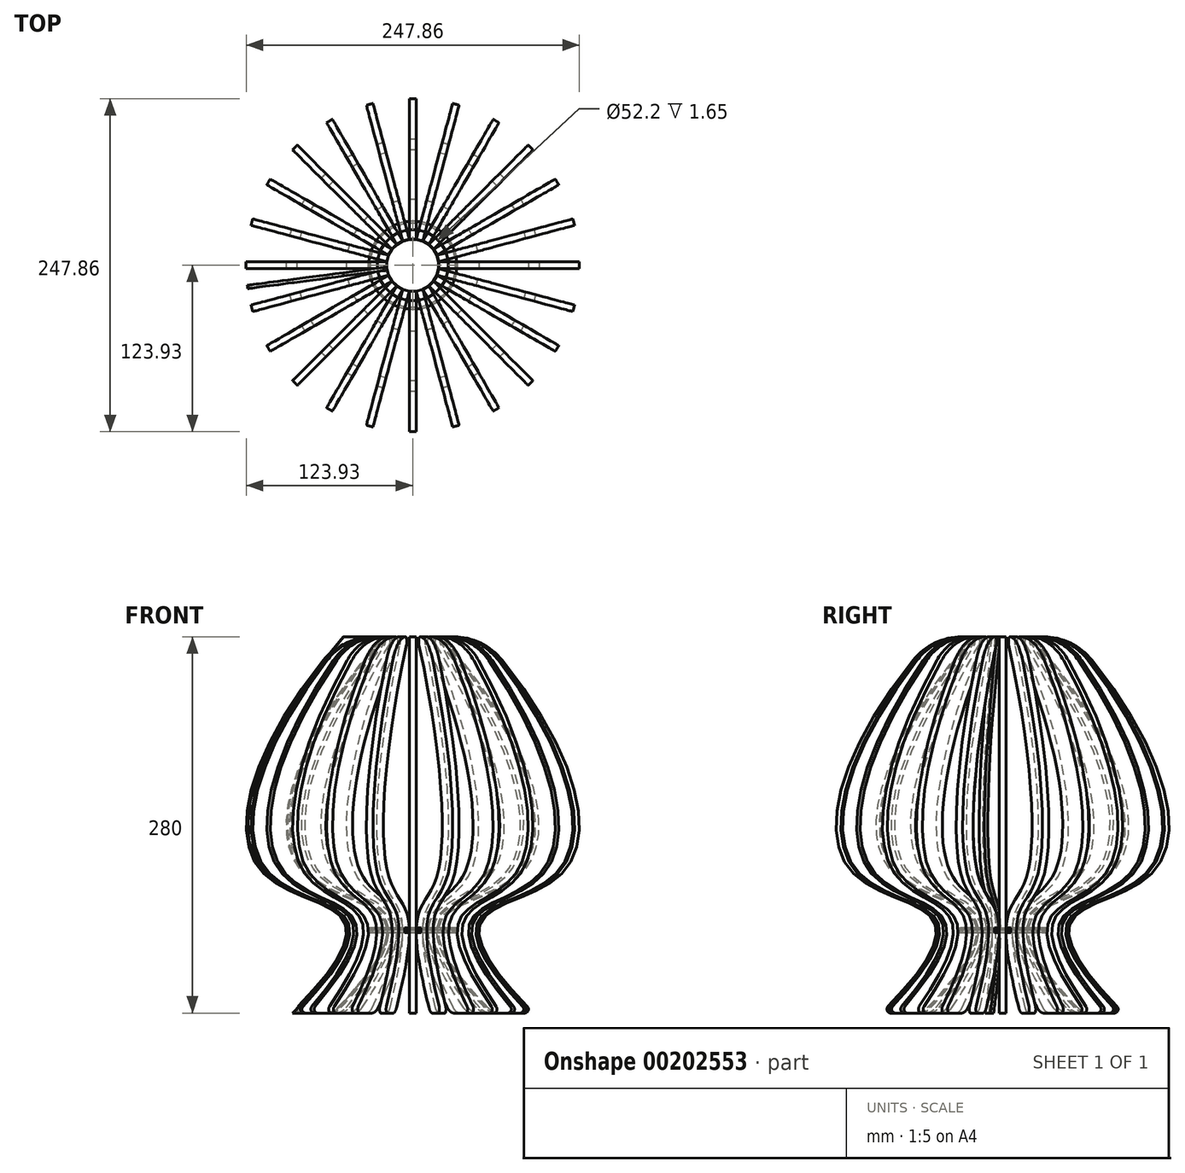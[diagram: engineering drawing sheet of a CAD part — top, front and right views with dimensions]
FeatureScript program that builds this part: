
annotation { "Feature Type Name" : "Feature", "Feature Type Description" : "" }
export const myFeature = defineFeature(function(context is Context, id is Id, definition is map)
    precondition{}
    {
        {
            var Q0;
            Q0=qCreatedBy(makeId("Top.planeOp"),FACE);
            var sketch = newSketch(context, id + "F0", { "sketchPlane" : qUnion([Q0])});
            skCircle(sketch, "E0", {"center": v(0, 0) * mm, "radius": 32.75 * mm});
            skCircle(sketch, "E1", {"center": v(0, 0) * mm, "radius": 26.1 * mm});
            skSolve(sketch);
        }
        {
            var Q0;
            Q0=qSketchRegion(id+"F0",true);
            extrude(context, id + "F1", {"entities" : qUnion([Q0]), "depth" : 1.65 * mm});
        }
        {
            var Q0;
            Q0=makeQuery(id+"F1.opExtrude","CAP_FACE",FACE,{"disambiguationData":[OSD([sQuery(id+"F0.wireOp",EDGE,"E0"),sQuery(id+"F0.wireOp",EDGE,"E1")])],"isStart":false});
            var sketch = newSketch(context, id + "F2", { "sketchPlane" : qUnion([Q0])});
            skLineSegment(sketch, "E2.bottom", {"start": v(2.5, -26.5) * mm, "end": v(-2.5, -26.5) * mm});
            skLineSegment(sketch, "E2.top", {"start": v(2.5, -31.5) * mm, "end": v(-2.5, -31.5) * mm});
            skLineSegment(sketch, "E2.left", {"start": v(2.5, -26.5) * mm, "end": v(2.5, -31.5) * mm});
            skLineSegment(sketch, "E2.right", {"start": v(-2.5, -26.5) * mm, "end": v(-2.5, -31.5) * mm});
            skPoint(sketch, "E2.middle", {"position": v(0, -29) * mm});
            skSolve(sketch);
        }
        {
            var Q0;
            Q0=makeQuery(id+"F2.imprint","IMPRINT",FACE,{"disambiguationData":[TD([[makeQuery(id+"F2.imprint","IMPRINT",EDGE,{"derivedFrom":sQuery(id+"F2.wireOp",EDGE,"E2.bottom")}),1.0]])]});
            extrude(context, id + "F3", {"entities" : qUnion([Q0]), "depth" : 1.62 * mm});
        }
        {
            var Q0;
            Q0=makeQuery(id+"F3.opExtrude","SWEPT_BODY",BODY,{"disambiguationData":[OSD([sQuery(id+"F2.wireOp",EDGE,"E2.bottom"),sQuery(id+"F2.wireOp",EDGE,"E2.top"),sQuery(id+"F2.wireOp",EDGE,"E2.left"),sQuery(id+"F2.wireOp",EDGE,"E2.right")])]});
            var Q1;
            Q1=makeQuery(id+"F1.opExtrude","CAP_EDGE",EDGE,{"disambiguationData":[OSD([sQuery(id+"F0.wireOp",EDGE,"E0")])],"isStart":false});
            circularPattern(context, id + "F4", {"entities" : qUnion([Q0]), "axis" : qUnion([Q1]), "angle" : 360 * degree, "instanceCount" : 24, "equalSpace" : true});
        }
        {
            var Q0;
            Q0=qCreatedBy(makeId("Front.planeOp"),FACE);
            var sketch = newSketch(context, id + "F5", { "sketchPlane" : qUnion([Q0])});
            skFitSpline(sketch, "E3", {"points": [v(-52, 220) * mm, v(-112, 45) * mm, v(-52, 10) * mm, v(-90, -60) * mm], "startDerivative": vector(-464.56, -534.92) * mm, "endDerivative": vector(-310.1, -311.21) * mm});
            skLineSegment(sketch, "E4", {"start": v(-9.97, -59.99) * mm, "end": v(-9.97, -0.01) * mm, "construction": true});
            skLineSegment(sketch, "E5", {"start": v(-9.97, -0.01) * mm, "end": v(-33, -0.01) * mm});
            skLineSegment(sketch, "E6", {"start": v(-33, -0.01) * mm, "end": v(-33, 3.46) * mm});
            skLineSegment(sketch, "E7", {"start": v(-33, 3.46) * mm, "end": v(0, 3.46) * mm});
            skLineSegment(sketch, "E8", {"start": v(0, 3.46) * mm, "end": v(0, 369.62) * mm, "construction": true});
            skLineSegment(sketch, "E9", {"start": v(-22, 3.46) * mm, "end": v(-22, 220) * mm, "construction": true});
            skFitSpline(sketch, "E10", {"points": [v(-60, -60) * mm, v(-22, 10) * mm, v(-82, 45) * mm, v(-22, 220) * mm], "startDerivative": vector(310.1, 311.21) * mm, "endDerivative": vector(464.56, 534.92) * mm});
            skLineSegment(sketch, "E11", {"start": v(-90, -60) * mm, "end": v(-60, -60) * mm});
            skLineSegment(sketch, "E12", {"start": v(-60.1, -30) * mm, "end": v(-30.1, -30) * mm, "construction": true});
            skLineSegment(sketch, "E13", {"start": v(-52, 10) * mm, "end": v(-22, 10) * mm, "construction": true});
            skLineSegment(sketch, "E14", {"start": v(-52, 220) * mm, "end": v(-22, 220) * mm});
            skLineSegment(sketch, "E15", {"start": v(-120.25, 141.41) * mm, "end": v(-90.25, 141.41) * mm, "construction": true});
            skLineSegment(sketch, "E16", {"start": v(-112, 45) * mm, "end": v(-82, 45) * mm, "construction": true});
            skPoint(sketch, "E17", {"position": v(-9.97, -30) * mm});
            skSolve(sketch);
        }
        {
            var Q0;
            Q0=makeQuery(id+"F5.imprint","IMPRINT",FACE,{"disambiguationData":[TD([[makeQuery(id+"F5.imprint","IMPRINT",EDGE,{"derivedFrom":sQuery(id+"F5.wireOp",EDGE,"E3")}),1.0]])]});
            extrude(context, id + "F6", {"entities" : qUnion([Q0]), "endBound" : BoundingType.SYMMETRIC, "depth" : 5 * mm});
        }
        {
            var Q0;
            Q0=makeQuery(id+"F6.opExtrude","SWEPT_EDGE",EDGE,{"disambiguationData":[OSD([sQuery(id+"F5.wireOp",EDGE,"E3"),sQuery(id+"F5.wireOp",EDGE,"E14")])]});
            fillet(context, id + "F7", {"entities" : qUnion([Q0]), "radius" : 46.48 * mm, "tangentPropagation" : true, "allowEdgeOverflow" : false});
        }
        {
            var Q0;
            Q0=makeQuery(id+"F6.opExtrude","SWEPT_EDGE",EDGE,{"disambiguationData":[OSD([sQuery(id+"F5.wireOp",EDGE,"E10"),sQuery(id+"F5.wireOp",EDGE,"E14")])]});
            fillet(context, id + "F8", {"entities" : qUnion([Q0]), "radius" : 3.7 * mm, "tangentPropagation" : true, "allowEdgeOverflow" : false});
        }
        {
            var Q0;
            Q0=makeQuery(id+"F6.opExtrude","SWEPT_EDGE",EDGE,{"disambiguationData":[OSD([sQuery(id+"F5.wireOp",EDGE,"E3"),sQuery(id+"F5.wireOp",EDGE,"E11")])]});
            fillet(context, id + "F9", {"entities" : qUnion([Q0]), "radius" : 2.86 * mm, "tangentPropagation" : true, "allowEdgeOverflow" : false});
        }
        {
            var Q0;
            Q0=makeQuery(id+"F6.opExtrude","SWEPT_EDGE",EDGE,{"disambiguationData":[OSD([sQuery(id+"F5.wireOp",EDGE,"E10"),sQuery(id+"F5.wireOp",EDGE,"E11")])]});
            fillet(context, id + "F10", {"entities" : qUnion([Q0]), "radius" : 13.3 * mm, "tangentPropagation" : true, "allowEdgeOverflow" : false});
        }
        {
            var Q0;
            Q0=makeQuery(id+"F6.opExtrude","SWEPT_BODY",BODY,{"disambiguationData":[OSD([sQuery(id+"F5.wireOp",EDGE,"E3"),sQuery(id+"F5.wireOp",EDGE,"E5"),sQuery(id+"F5.wireOp",EDGE,"E6"),sQuery(id+"F5.wireOp",EDGE,"E7"),sQuery(id+"F5.wireOp",EDGE,"E10"),sQuery(id+"F5.wireOp",EDGE,"E11"),sQuery(id+"F5.wireOp",EDGE,"E14")])]});
            var Q1;
            Q1=sQuery(id+"F5.wireOp",EDGE,"E8");
            circularPattern(context, id + "F11", {"entities" : qUnion([Q0]), "axis" : qUnion([Q1]), "angle" : 360 * degree, "instanceCount" : 24, "equalSpace" : true});
        }
        {
            var Q0;
            Q0=qCreatedBy(makeId("Top.planeOp"),FACE);
            var sketch = newSketch(context, id + "F12", { "sketchPlane" : qUnion([Q0])});
            skCircle(sketch, "E18", {"center": v(0, 0) * mm, "radius": 55.99 * mm});
            skCircle(sketch, "E19", {"center": v(0, 0) * mm, "radius": 18.7 * mm});
            skCircle(sketch, "E20", {"center": v(0, 0) * mm, "radius": 37.24 * mm});
            skSolve(sketch);
        }
        {
            var Q0;
            Q0=makeQuery(id+"F6.opExtrude","SWEPT_FACE",FACE,{"disambiguationData":[OSD([sQuery(id+"F5.wireOp",EDGE,"E11")])]});
            var sketch = newSketch(context, id + "F13", { "sketchPlane" : qUnion([Q0])});
            skCircle(sketch, "E21", {"center": v(0, 0) * mm, "radius": 83.18 * mm});
            skSolve(sketch);
        }
        {
            var Q0;
            Q0=sQuery(id+"F12.wireOp",EDGE,"E20");
            var Q1;
            Q1=sQuery(id+"F13.wireOp",EDGE,"E21");
            loft(context, id + "F14", {"bodyType" : ToolBodyType.SURFACE, "wireProfilesArray" : [{ "wireProfileEntities" : qUnion([Q0]) }, { "wireProfileEntities" : qUnion([Q1]) }]});
        }
        {
            var Q0;
            Q0=makeQuery(id+"F5.imprint","IMPRINT",FACE,{"disambiguationData":[TD([[makeQuery(id+"F5.imprint","IMPRINT",EDGE,{"derivedFrom":sQuery(id+"F5.wireOp",EDGE,"E3")}),1.0]])]});
            extrude(context, id + "F15", {"entities" : qUnion([Q0]), "endBound" : BoundingType.SYMMETRIC, "depth" : 2.5 * mm});
        }
        {
            var Q0;
            Q0=makeQuery(id+"F15.opExtrude","SWEPT_BODY",BODY,{"disambiguationData":[OSD([sQuery(id+"F5.wireOp",EDGE,"E3"),sQuery(id+"F5.wireOp",EDGE,"E5"),sQuery(id+"F5.wireOp",EDGE,"E6"),sQuery(id+"F5.wireOp",EDGE,"E7"),sQuery(id+"F5.wireOp",EDGE,"E10"),sQuery(id+"F5.wireOp",EDGE,"E11"),sQuery(id+"F5.wireOp",EDGE,"E14")])]});
            var Q1;
            Q1=sQuery(id+"F5.wireOp",EDGE,"E8");
            transform(context, id + "F16", {"entities" : qUnion([Q0]), "transformType" : TransformType.ROTATION, "transformAxis" : qUnion([Q1]), "angle" : 7.5 * degree, "makeCopy" : false});
        }
    });
